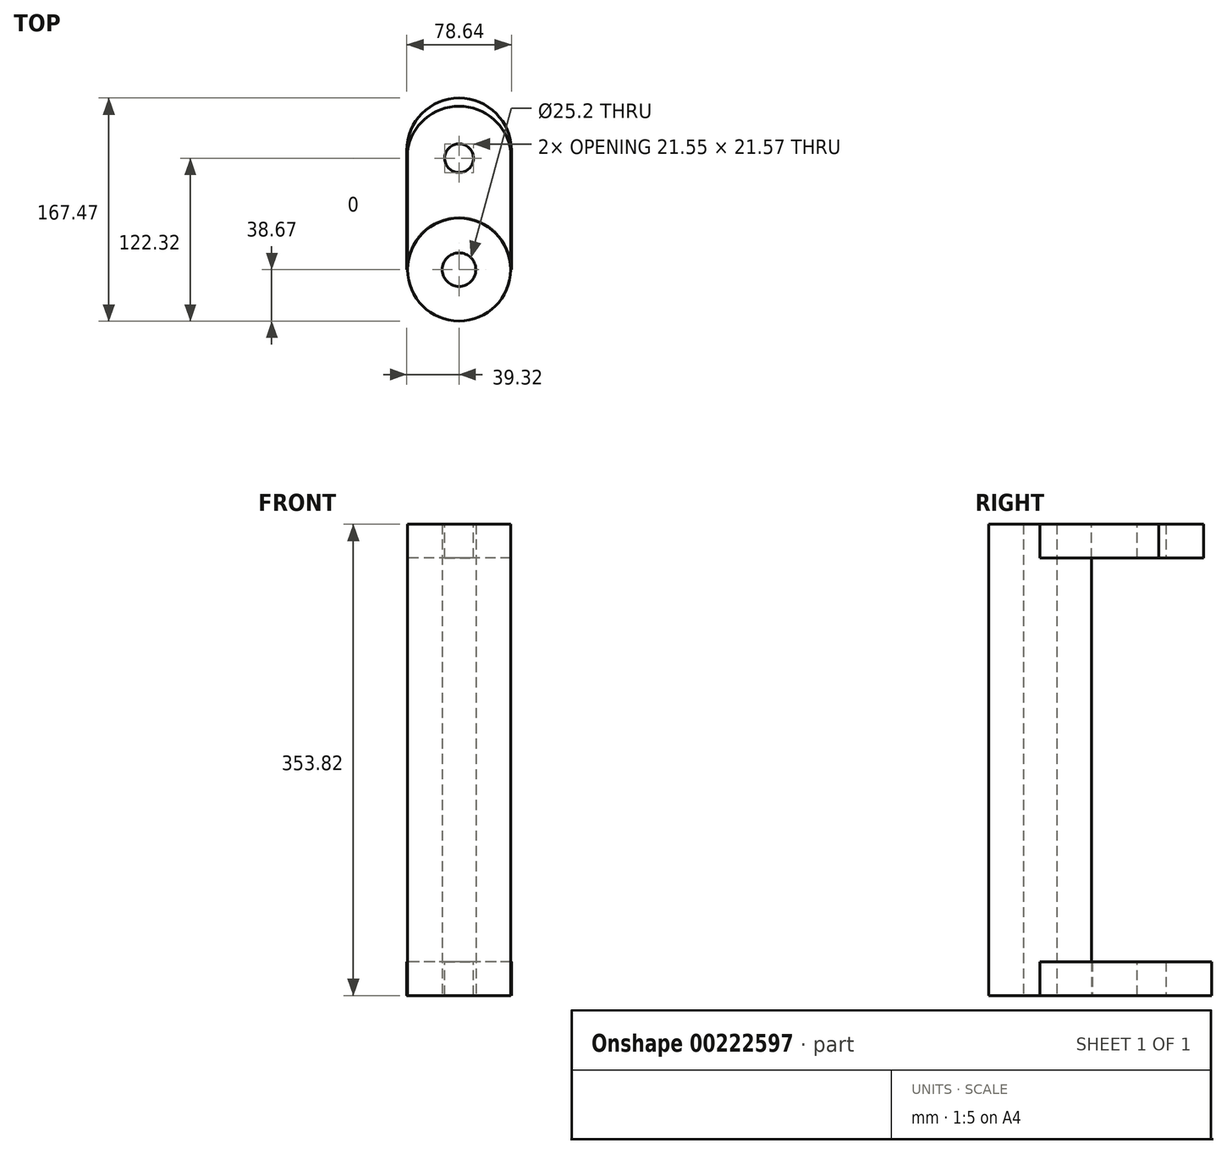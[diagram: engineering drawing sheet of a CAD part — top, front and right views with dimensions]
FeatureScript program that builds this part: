
annotation { "Feature Type Name" : "Feature", "Feature Type Description" : "" }
export const myFeature = defineFeature(function(context is Context, id is Id, definition is map)
    precondition{}
    {
        {
            var Q0;
            Q0=qCreatedBy(makeId("Top.planeOp"),FACE);
            var sketch = newSketch(context, id + "F0", { "sketchPlane" : qUnion([Q0])});
            skCircle(sketch, "E0", {"center": v(0, 0) * mm, "radius": 38.67 * mm});
            skSolve(sketch);
        }
        {
            var Q0;
            Q0 = qSketchRegion(id + "F0", true);
            extrude(context, id + "F1", {"entities" : qUnion([Q0]), "depth" : 353.82 * mm});
        }
        {
            var Q0;
            Q0=qCreatedBy(makeId("Top.planeOp"),FACE);
            var sketch = newSketch(context, id + "F2", { "sketchPlane" : qUnion([Q0])});
            skCircle(sketch, "E1", {"center": v(0, 0) * mm, "radius": 12.6 * mm});
            skSolve(sketch);
        }
        {
            var Q0;
            Q0 = qSketchRegion(id + "F2", true);
            extrude(context, id + "F3", {"entities" : qUnion([Q0]), "operationType" : NewBodyOperationType.REMOVE, "endBound" : BoundingType.THROUGH_ALL, "depth" : 25.4 * mm});
        }
        {
            var Q0;
            Q0=qCreatedBy(makeId("Top.planeOp"),FACE);
            var sketch = newSketch(context, id + "F4", { "sketchPlane" : qUnion([Q0])});
            skLineSegment(sketch, "E2", {"start": v(-39.32, 0) * mm, "end": v(-39.32, 75.78) * mm});
            skLineSegment(sketch, "E3", {"start": v(39.32, 0) * mm, "end": v(39.32, 75.78) * mm});
            skArc(sketch, "E4", {"start": v(39.32, 0) * mm, "mid": v(0, 39.32) * mm, "end": v(-39.32, 0) * mm});
            skLineSegment(sketch, "E5", {"start": v(-39.32, 75.78) * mm, "end": v(-39.32, 89.47) * mm});
            skLineSegment(sketch, "E6", {"start": v(39.32, 75.78) * mm, "end": v(39.32, 89.47) * mm});
            skArc(sketch, "E7", {"start": v(39.32, 89.47) * mm, "mid": v(0, 128.8) * mm, "end": v(-39.32, 89.47) * mm});
            skSolve(sketch);
        }
        {
            var Q0;
            Q0=makeQuery(id+"F4.imprint","IMPRINT",FACE,{"disambiguationData":[TD([[makeQuery(id+"F4.imprint","IMPRINT",EDGE,{"derivedFrom":sQuery(id+"F4.wireOp",EDGE,"E2")}),-1.0]])]});
            extrude(context, id + "F5", {"entities" : qUnion([Q0]), "depth" : 25.4 * mm});
        }
        {
            var Q0;
            Q0=makeQuery(id+"F1.opExtrude","CAP_FACE",FACE,{"disambiguationData":[OSD([sQuery(id+"F0.wireOp",EDGE,"E0")])],"isStart":false});
            var sketch = newSketch(context, id + "F6", { "sketchPlane" : qUnion([Q0])});
            skLineSegment(sketch, "E8", {"start": v(-38.67, 0) * mm, "end": v(-38.67, 89.21) * mm});
            skLineSegment(sketch, "E9", {"start": v(38.67, 0) * mm, "end": v(38.67, 89.21) * mm});
            skArc(sketch, "E10", {"start": v(38.67, 0) * mm, "mid": v(0, 38.67) * mm, "end": v(-38.67, 0) * mm});
            skArc(sketch, "E11", {"start": v(38.67, 89.21) * mm, "mid": v(0, 122.72) * mm, "end": v(-38.67, 89.21) * mm});
            skSolve(sketch);
        }
        {
            var Q0;
            Q0 = qSketchRegion(id + "F6", true);
            extrude(context, id + "F7", {"entities" : qUnion([Q0]), "oppositeDirection" : true, "depth" : 25.4 * mm});
        }
        {
            var Q0;
            Q0=makeQuery(id+"F7.opExtrude","CAP_FACE",FACE,{"disambiguationData":[OSD([sQuery(id+"F6.wireOp",EDGE,"E8"),sQuery(id+"F6.wireOp",EDGE,"E9"),sQuery(id+"F6.wireOp",EDGE,"E10"),sQuery(id+"F6.wireOp",EDGE,"E11")])],"isStart":true});
            var sketch = newSketch(context, id + "F8", { "sketchPlane" : qUnion([Q0])});
            skCircle(sketch, "E12", {"center": v(0, 83.65) * mm, "radius": 10.78 * mm});
            skSolve(sketch);
        }
        {
            var Q0;
            Q0 = qSketchRegion(id + "F8", true);
            extrude(context, id + "F9", {"entities" : qUnion([Q0]), "operationType" : NewBodyOperationType.REMOVE, "endBound" : BoundingType.THROUGH_ALL, "oppositeDirection" : true, "depth" : 25.4 * mm});
        }
        {
            var Q0;
            Q0=makeQuery(id+"F5.opExtrude","CAP_FACE",FACE,{"disambiguationData":[OSD([sQuery(id+"F4.wireOp",EDGE,"E2"),sQuery(id+"F4.wireOp",EDGE,"E3"),sQuery(id+"F4.wireOp",EDGE,"E4"),sQuery(id+"F4.wireOp",EDGE,"E5"),sQuery(id+"F4.wireOp",EDGE,"E6"),sQuery(id+"F4.wireOp",EDGE,"E7")])],"isStart":true});
            var sketch = newSketch(context, id + "F10", { "sketchPlane" : qUnion([Q0])});
            skCircle(sketch, "E13", {"center": v(0, -84.43) * mm, "radius": 10 * mm});
            skSolve(sketch);
        }
        {
            var Q0;
            Q0 = qSketchRegion(id + "F10", true);
            extrude(context, id + "F11", {"entities" : qUnion([Q0]), "operationType" : NewBodyOperationType.REMOVE, "endBound" : BoundingType.THROUGH_ALL, "oppositeDirection" : true, "depth" : 25.4 * mm});
        }
    });
